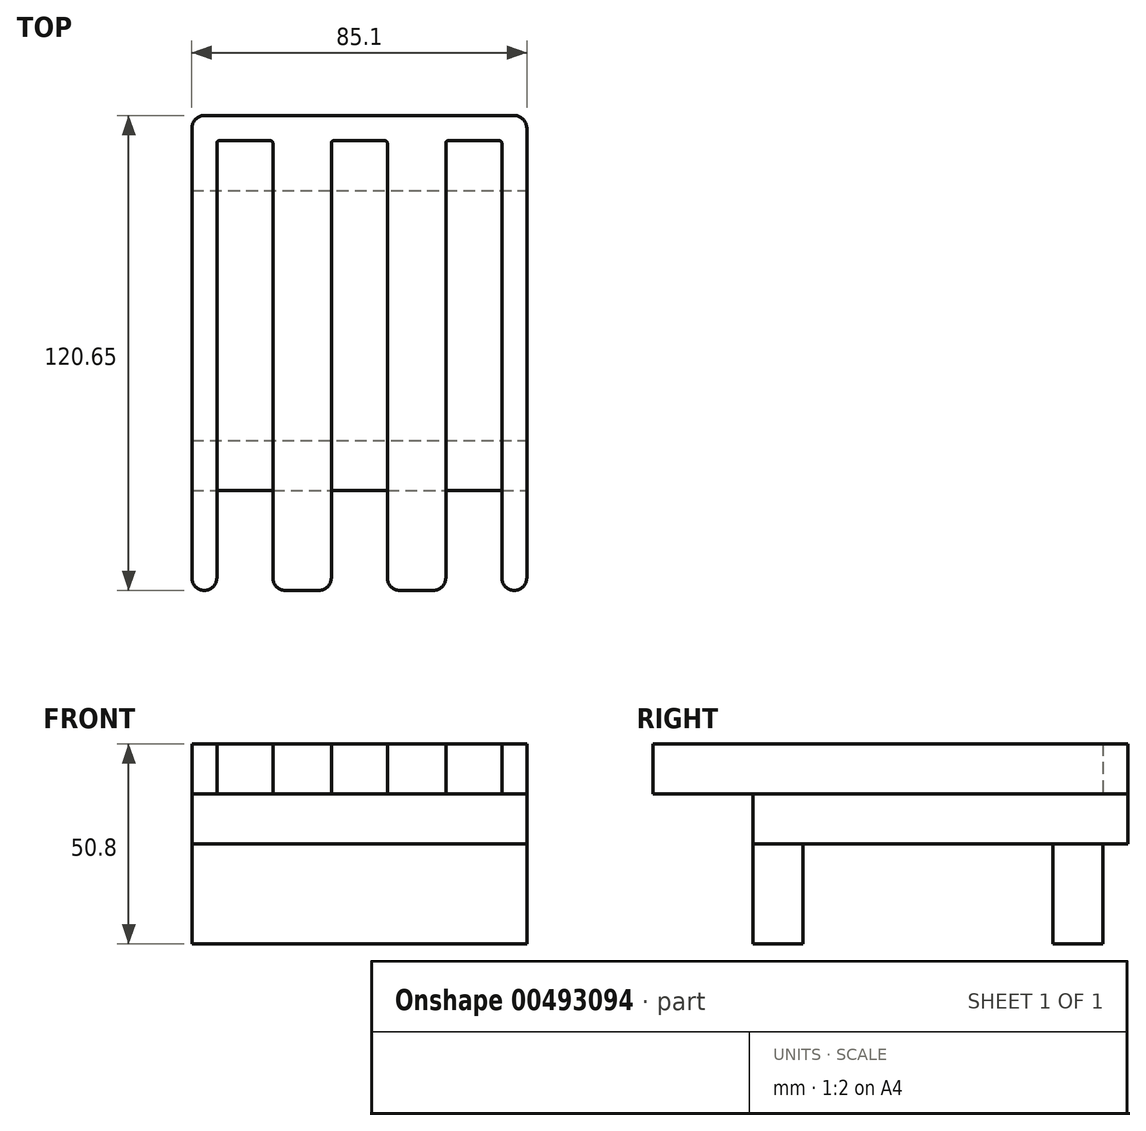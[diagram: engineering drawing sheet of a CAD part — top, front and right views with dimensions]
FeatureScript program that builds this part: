
annotation { "Feature Type Name" : "Feature", "Feature Type Description" : "" }
export const myFeature = defineFeature(function(context is Context, id is Id, definition is map)
    precondition{}
    {
        {
            var Q0;
            Q0=qCreatedBy(makeId("Top.planeOp"),FACE);
            var sketch = newSketch(context, id + "F0", { "sketchPlane" : qUnion([Q0])});
            skLineSegment(sketch, "E0.bottom", {"start": v(-42.55, 47.63) * mm, "end": v(42.55, 47.63) * mm});
            skLineSegment(sketch, "E0.top", {"start": v(-42.55, -47.63) * mm, "end": v(42.55, -47.63) * mm});
            skLineSegment(sketch, "E0.left", {"start": v(-42.55, 47.63) * mm, "end": v(-42.55, -47.63) * mm});
            skLineSegment(sketch, "E0.right", {"start": v(42.55, 47.63) * mm, "end": v(42.55, -47.63) * mm});
            skPoint(sketch, "E0.middle", {"position": v(0, 0) * mm});
            skSolve(sketch);
        }
        {
            var Q0;
            Q0=qSketchRegion(id+"F0",true);
            extrude(context, id + "F1", {"entities" : qUnion([Q0]), "depth" : 12.7 * mm});
        }
        {
            var Q0;
            Q0=makeQuery(id+"F1.opExtrude","CAP_FACE",FACE,{"disambiguationData":[OSD([sQuery(id+"F0.wireOp",EDGE,"E0.bottom"),sQuery(id+"F0.wireOp",EDGE,"E0.top"),sQuery(id+"F0.wireOp",EDGE,"E0.left"),sQuery(id+"F0.wireOp",EDGE,"E0.right")])],"isStart":false});
            var sketch = newSketch(context, id + "F2", { "sketchPlane" : qUnion([Q0])});
            skLineSegment(sketch, "E1.bottom", {"start": v(21.97, 41.28) * mm, "end": v(36.2, 41.28) * mm});
            skLineSegment(sketch, "E1.left", {"start": v(21.97, 41.28) * mm, "end": v(21.97, -73.03) * mm});
            skLineSegment(sketch, "E1.right", {"start": v(36.2, 41.28) * mm, "end": v(36.2, -73.03) * mm});
            skLineSegment(sketch, "E2", {"start": v(0, 47.63) * mm, "end": v(0, -47.63) * mm, "construction": true});
            skLineSegment(sketch, "E3.MirrorCS", {"start": v(-21.97, 41.28) * mm, "end": v(-21.97, -73.03) * mm});
            skLineSegment(sketch, "E4.MirrorCS", {"start": v(-21.97, 41.28) * mm, "end": v(-36.2, 41.28) * mm});
            skLineSegment(sketch, "E5.MirrorCS", {"start": v(-36.2, 41.28) * mm, "end": v(-36.2, -73.03) * mm});
            skLineSegment(sketch, "E6.bottom", {"start": v(-7.11, 41.28) * mm, "end": v(7.11, 41.28) * mm});
            skLineSegment(sketch, "E6.left", {"start": v(-7.11, 41.28) * mm, "end": v(-7.11, -73.03) * mm});
            skLineSegment(sketch, "E6.right", {"start": v(7.11, 41.28) * mm, "end": v(7.11, -73.03) * mm});
            skPoint(sketch, "E7", {"position": v(0, 41.28) * mm});
            skLineSegment(sketch, "E8.bottom", {"start": v(-42.55, 47.63) * mm, "end": v(42.55, 47.63) * mm});
            skLineSegment(sketch, "E8.top", {"start": v(-42.54, -73.03) * mm, "end": v(-36.2, -73.03) * mm});
            skLineSegment(sketch, "E8.left", {"start": v(-42.55, 47.62) * mm, "end": v(-42.55, -73.03) * mm});
            skLineSegment(sketch, "E8.right", {"start": v(42.55, 47.62) * mm, "end": v(42.55, -73.03) * mm});
            skLineSegment(sketch, "E9.trimOffspring", {"start": v(-21.97, -73.03) * mm, "end": v(-7.11, -73.03) * mm});
            skLineSegment(sketch, "E10.trimOffspring", {"start": v(7.11, -73.03) * mm, "end": v(21.97, -73.03) * mm});
            skLineSegment(sketch, "E11.trimOffspring", {"start": v(36.2, -73.03) * mm, "end": v(42.55, -73.03) * mm});
            skPoint(sketch, "E12.orphan", {"position": v(-36.2, -85.72) * mm});
            skPoint(sketch, "E13.MirrorCS.start.orphan", {"position": v(-21.97, -85.72) * mm});
            skPoint(sketch, "E14.orphan", {"position": v(7.11, -85.72) * mm});
            skPoint(sketch, "E1.top.start.orphan", {"position": v(21.97, -85.72) * mm});
            skPoint(sketch, "E15.orphan", {"position": v(36.2, -85.72) * mm});
            skSolve(sketch);
        }
        {
            var Q0;
            Q0=qSketchRegion(id+"F2",true);
            extrude(context, id + "F3", {"entities" : qUnion([Q0]), "depth" : 12.7 * mm});
        }
        {
            var Q0;
            Q0=makeQuery(id+"F1.opExtrude","CAP_FACE",FACE,{"disambiguationData":[OSD([sQuery(id+"F0.wireOp",EDGE,"E0.bottom"),sQuery(id+"F0.wireOp",EDGE,"E0.top"),sQuery(id+"F0.wireOp",EDGE,"E0.left"),sQuery(id+"F0.wireOp",EDGE,"E0.right")])],"isStart":true});
            var sketch = newSketch(context, id + "F4", { "sketchPlane" : qUnion([Q0])});
            skLineSegment(sketch, "E16.bottom", {"start": v(-42.55, 47.63) * mm, "end": v(42.55, 47.63) * mm});
            skLineSegment(sketch, "E16.top", {"start": v(-42.55, 34.93) * mm, "end": v(42.55, 34.93) * mm});
            skLineSegment(sketch, "E16.left", {"start": v(-42.55, 47.63) * mm, "end": v(-42.55, 34.93) * mm});
            skLineSegment(sketch, "E16.right", {"start": v(42.55, 47.63) * mm, "end": v(42.55, 34.93) * mm});
            skLineSegment(sketch, "E17.bottom", {"start": v(-42.55, -41.28) * mm, "end": v(42.55, -41.28) * mm});
            skLineSegment(sketch, "E17.top", {"start": v(-42.55, -28.58) * mm, "end": v(42.55, -28.58) * mm});
            skLineSegment(sketch, "E17.left", {"start": v(-42.55, -41.28) * mm, "end": v(-42.55, -28.58) * mm});
            skLineSegment(sketch, "E17.right", {"start": v(42.55, -41.28) * mm, "end": v(42.55, -28.58) * mm});
            skSolve(sketch);
        }
        {
            var Q0;
            Q0=qSketchRegion(id+"F4",true);
            extrude(context, id + "F5", {"entities" : qUnion([Q0]), "depth" : 25.4 * mm});
        }
        {
            var Q0;
            Q0=makeQuery(id+"F3.opExtrude","SWEPT_EDGE",EDGE,{"disambiguationData":[OSD([sQuery(id+"F2.wireOp",EDGE,"E5.MirrorCS"),sQuery(id+"F2.wireOp",EDGE,"E8.top")])]});
            var Q1;
            Q1=makeQuery(id+"F3.opExtrude","SWEPT_EDGE",EDGE,{"disambiguationData":[OSD([sQuery(id+"F2.wireOp",EDGE,"E8.top"),sQuery(id+"F2.wireOp",EDGE,"E8.left")])]});
            var Q2;
            Q2=makeQuery(id+"F3.opExtrude","SWEPT_EDGE",EDGE,{"disambiguationData":[OSD([sQuery(id+"F2.wireOp",EDGE,"E3.MirrorCS"),sQuery(id+"F2.wireOp",EDGE,"E9.trimOffspring")])]});
            var Q3;
            Q3=makeQuery(id+"F3.opExtrude","SWEPT_EDGE",EDGE,{"disambiguationData":[OSD([sQuery(id+"F2.wireOp",EDGE,"E6.left"),sQuery(id+"F2.wireOp",EDGE,"E9.trimOffspring")])]});
            var Q4;
            Q4=makeQuery(id+"F3.opExtrude","SWEPT_EDGE",EDGE,{"disambiguationData":[OSD([sQuery(id+"F2.wireOp",EDGE,"E6.right"),sQuery(id+"F2.wireOp",EDGE,"E10.trimOffspring")])]});
            var Q5;
            Q5=makeQuery(id+"F3.opExtrude","SWEPT_EDGE",EDGE,{"disambiguationData":[OSD([sQuery(id+"F2.wireOp",EDGE,"E1.left"),sQuery(id+"F2.wireOp",EDGE,"E10.trimOffspring")])]});
            var Q6;
            Q6=makeQuery(id+"F3.opExtrude","SWEPT_EDGE",EDGE,{"disambiguationData":[OSD([sQuery(id+"F2.wireOp",EDGE,"E8.right"),sQuery(id+"F2.wireOp",EDGE,"E11.trimOffspring")])]});
            var Q7;
            Q7=makeQuery(id+"F3.opExtrude","SWEPT_EDGE",EDGE,{"disambiguationData":[OSD([sQuery(id+"F2.wireOp",EDGE,"E8.bottom"),sQuery(id+"F2.wireOp",EDGE,"E8.right")])]});
            var Q8;
            Q8=makeQuery(id+"F1.opExtrude","SWEPT_EDGE",EDGE,{"disambiguationData":[OSD([sQuery(id+"F0.wireOp",EDGE,"E0.bottom"),sQuery(id+"F0.wireOp",EDGE,"E0.right")])]});
            var Q9;
            Q9=makeQuery(id+"F3.opExtrude","SWEPT_EDGE",EDGE,{"disambiguationData":[OSD([sQuery(id+"F2.wireOp",EDGE,"E8.bottom"),sQuery(id+"F2.wireOp",EDGE,"E8.left")])]});
            var Q10;
            Q10=makeQuery(id+"F1.opExtrude","SWEPT_EDGE",EDGE,{"disambiguationData":[OSD([sQuery(id+"F0.wireOp",EDGE,"E0.bottom"),sQuery(id+"F0.wireOp",EDGE,"E0.left")])]});
            var Q11;
            Q11=makeQuery(id+"F3.opExtrude","SWEPT_EDGE",EDGE,{"disambiguationData":[OSD([sQuery(id+"F2.wireOp",EDGE,"E1.right"),sQuery(id+"F2.wireOp",EDGE,"E11.trimOffspring")])]});
            fillet(context, id + "F6", {"entities" : qUnion([Q0, Q1, Q2, Q3, Q4, Q5, Q6, Q7, Q8, Q9, Q10, Q11]), "radius" : 3.17 * mm, "tangentPropagation" : true, "allowEdgeOverflow" : false});
        }
        {
            var Q0;
            Q0=makeQuery(id+"F3.opExtrude","SWEPT_EDGE",EDGE,{"disambiguationData":[OSD([sQuery(id+"F2.wireOp",EDGE,"E4.MirrorCS"),sQuery(id+"F2.wireOp",EDGE,"E5.MirrorCS")])]});
            var Q1;
            Q1=makeQuery(id+"F3.opExtrude","SWEPT_EDGE",EDGE,{"disambiguationData":[OSD([sQuery(id+"F2.wireOp",EDGE,"E6.bottom"),sQuery(id+"F2.wireOp",EDGE,"E6.left")])]});
            var Q2;
            Q2=makeQuery(id+"F3.opExtrude","SWEPT_EDGE",EDGE,{"disambiguationData":[OSD([sQuery(id+"F2.wireOp",EDGE,"E1.bottom"),sQuery(id+"F2.wireOp",EDGE,"E1.left")])]});
            var Q3;
            Q3=makeQuery(id+"F3.opExtrude","SWEPT_EDGE",EDGE,{"disambiguationData":[OSD([sQuery(id+"F2.wireOp",EDGE,"E3.MirrorCS"),sQuery(id+"F2.wireOp",EDGE,"E4.MirrorCS")])]});
            var Q4;
            Q4=makeQuery(id+"F3.opExtrude","SWEPT_EDGE",EDGE,{"disambiguationData":[OSD([sQuery(id+"F2.wireOp",EDGE,"E6.bottom"),sQuery(id+"F2.wireOp",EDGE,"E6.right")])]});
            var Q5;
            Q5=makeQuery(id+"F3.opExtrude","SWEPT_EDGE",EDGE,{"disambiguationData":[OSD([sQuery(id+"F2.wireOp",EDGE,"E1.bottom"),sQuery(id+"F2.wireOp",EDGE,"E1.right")])]});
            fillet(context, id + "F7", {"entities" : qUnion([Q0, Q1, Q2, Q3, Q4, Q5]), "radius" : 0.64 * mm, "tangentPropagation" : true, "allowEdgeOverflow" : false});
        }
    });
